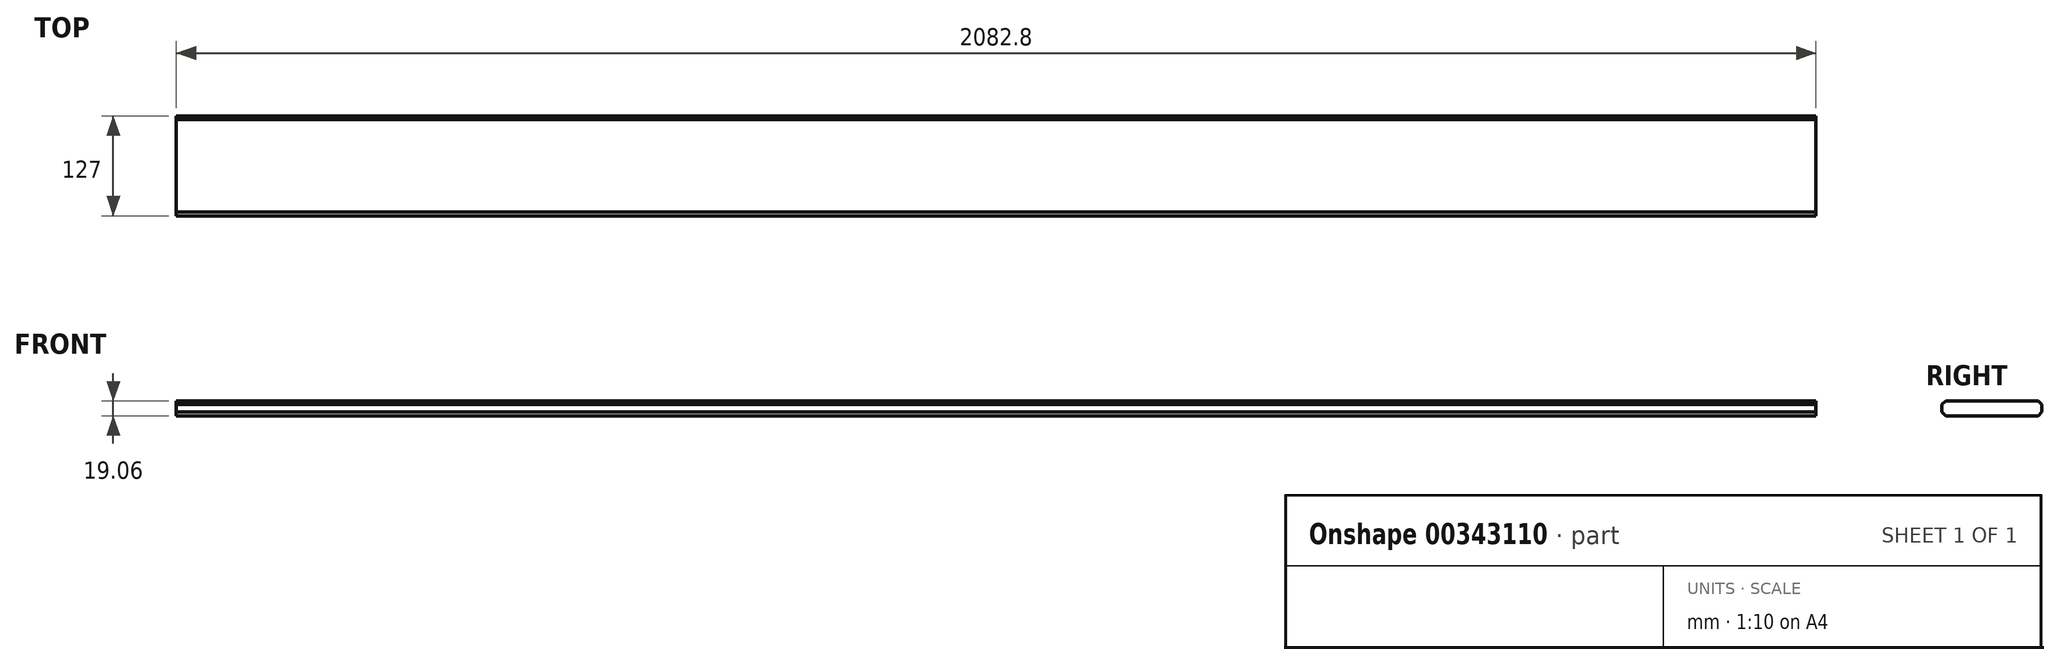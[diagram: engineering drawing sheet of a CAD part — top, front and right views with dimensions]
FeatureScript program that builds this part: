
annotation { "Feature Type Name" : "Feature", "Feature Type Description" : "" }
export const myFeature = defineFeature(function(context is Context, id is Id, definition is map)
    precondition{}
    {
        {
            var Q0;
            Q0=qCreatedBy(makeId("Right.planeOp"),FACE);
            var sketch = newSketch(context, id + "F0", { "sketchPlane" : qUnion([Q0])});
            skLineSegment(sketch, "E0.bottom", {"start": v(-63.5, 9.53) * mm, "end": v(63.5, 9.53) * mm});
            skLineSegment(sketch, "E0.top", {"start": v(-63.5, -9.52) * mm, "end": v(63.5, -9.52) * mm});
            skLineSegment(sketch, "E0.left", {"start": v(-63.5, 9.53) * mm, "end": v(-63.5, -9.52) * mm});
            skLineSegment(sketch, "E0.right", {"start": v(63.5, 9.53) * mm, "end": v(63.5, -9.52) * mm});
            skSolve(sketch);
        }
        {
            var Q0;
            Q0=makeQuery(id+"F0.imprint","IMPRINT",FACE,{"disambiguationData":[TD([[makeQuery(id+"F0.imprint","IMPRINT",EDGE,{"derivedFrom":sQuery(id+"F0.wireOp",EDGE,"E0.bottom")}),-1.0]])]});
            extrude(context, id + "F1", {"entities" : qUnion([Q0]), "endBound" : BoundingType.SYMMETRIC, "depth" : 2082.8 * mm});
        }
        {
            var Q0;
            Q0=makeQuery(id+"F1.opExtrude","SWEPT_EDGE",EDGE,{"disambiguationData":[OSD([sQuery(id+"F0.wireOp",EDGE,"E0.bottom"),sQuery(id+"F0.wireOp",EDGE,"E0.left")])]});
            var Q1;
            Q1=makeQuery(id+"F1.opExtrude","SWEPT_EDGE",EDGE,{"disambiguationData":[OSD([sQuery(id+"F0.wireOp",EDGE,"E0.top"),sQuery(id+"F0.wireOp",EDGE,"E0.left")])]});
            var Q2;
            Q2=makeQuery(id+"F1.opExtrude","SWEPT_EDGE",EDGE,{"disambiguationData":[OSD([sQuery(id+"F0.wireOp",EDGE,"E0.bottom"),sQuery(id+"F0.wireOp",EDGE,"E0.right")])]});
            var Q3;
            Q3=makeQuery(id+"F1.opExtrude","SWEPT_EDGE",EDGE,{"disambiguationData":[OSD([sQuery(id+"F0.wireOp",EDGE,"E0.top"),sQuery(id+"F0.wireOp",EDGE,"E0.right")])]});
            chamfer(context, id + "F2", {"entities" : qUnion([Q0, Q1, Q2, Q3]), "width" : 4.76 * mm, "tangentPropagation" : true});
        }
    });
